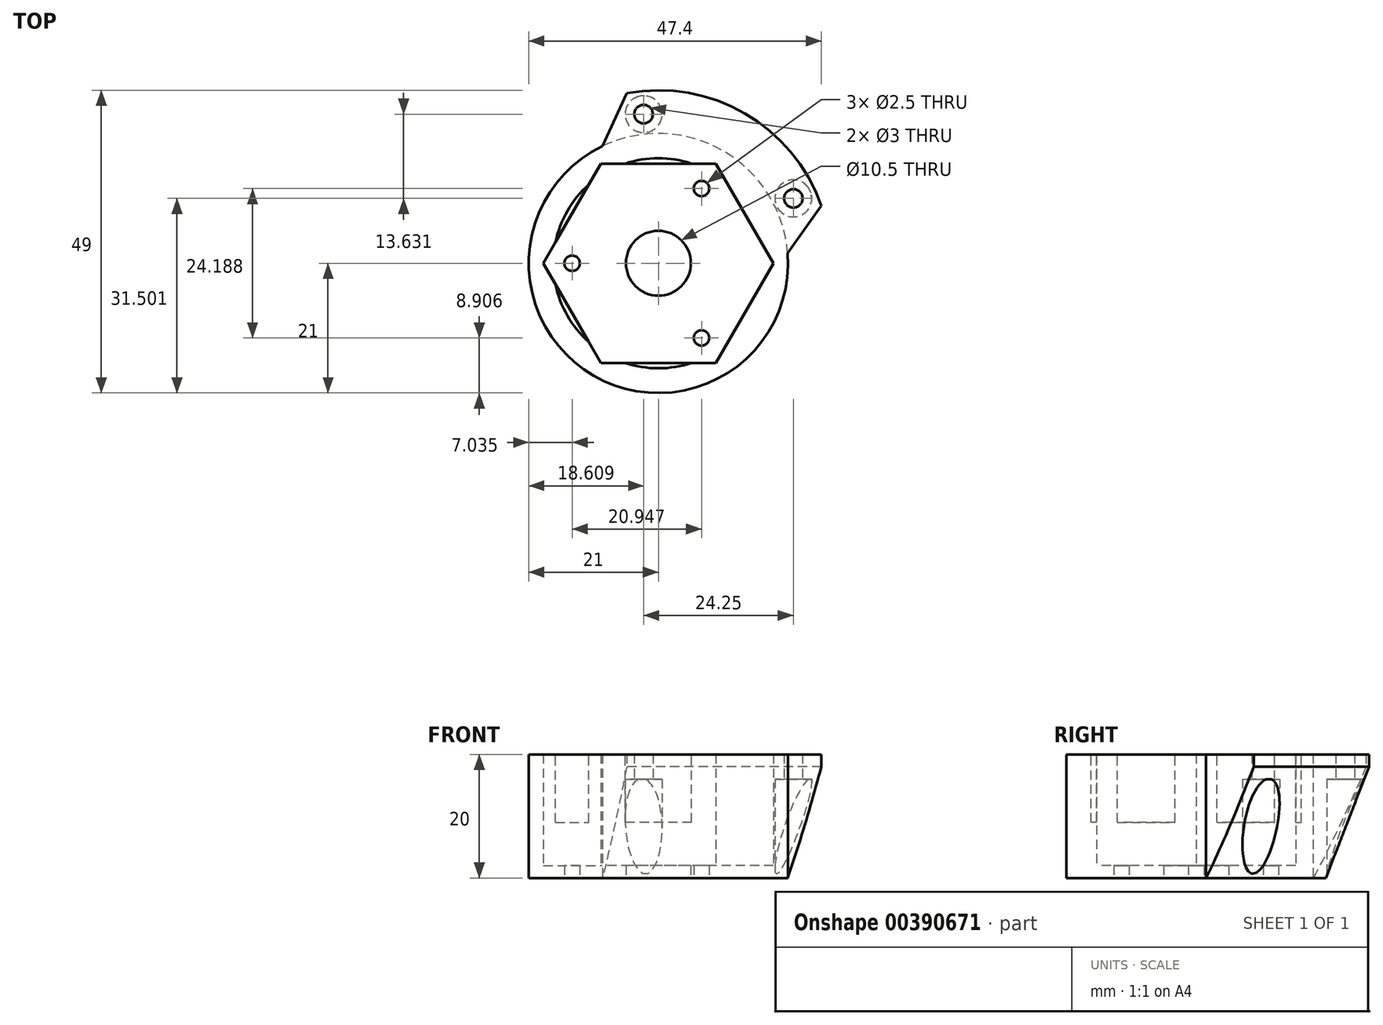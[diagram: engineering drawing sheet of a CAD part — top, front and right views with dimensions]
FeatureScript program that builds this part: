
annotation { "Feature Type Name" : "Feature", "Feature Type Description" : "" }
export const myFeature = defineFeature(function(context is Context, id is Id, definition is map)
    precondition{}
    {
        {
            var Q0;
            Q0=qCreatedBy(makeId("Top.planeOp"),FACE);
            var sketch = newSketch(context, id + "F0", { "sketchPlane" : qUnion([Q0])});
            skCircle(sketch, "E0.cCircle", {"center": v(0, 0) * mm, "radius": 16.12 * mm, "construction": true});
            skLineSegment(sketch, "E0.0", {"start": v(9.3, -16.12) * mm, "end": v(-9.3, -16.13) * mm});
            skLineSegment(sketch, "E0.1", {"start": v(-9.3, -16.12) * mm, "end": v(-18.62, 0) * mm});
            skLineSegment(sketch, "E0.2", {"start": v(-18.62, 0) * mm, "end": v(-9.3, 16.13) * mm});
            skLineSegment(sketch, "E0.3", {"start": v(-9.3, 16.12) * mm, "end": v(9.3, 16.13) * mm});
            skLineSegment(sketch, "E0.4", {"start": v(9.3, 16.12) * mm, "end": v(18.62, 0) * mm});
            skLineSegment(sketch, "E0.5", {"start": v(18.62, 0) * mm, "end": v(9.3, -16.13) * mm});
            skPoint(sketch, "E0.0.midPoint", {"position": v(0, -16.13) * mm});
            skCircle(sketch, "E1", {"center": v(0, 0) * mm, "radius": 5.25 * mm});
            skCircle(sketch, "E2", {"center": v(0, 0) * mm, "radius": 21 * mm});
            skCircle(sketch, "E3", {"center": v(0, 0) * mm, "radius": 28 * mm});
            skCircle(sketch, "E4", {"center": v(-13.96, 0) * mm, "radius": 1.25 * mm});
            skPoint(sketch, "E4.centerSnap0", {"position": v(-13.96, 8.06) * mm});
            skCircle(sketch, "E5.1.0", {"center": v(6.98, -12.1) * mm, "radius": 1.25 * mm});
            skCircle(sketch, "E5.2.0", {"center": v(6.98, 12.1) * mm, "radius": 1.25 * mm});
            skPoint(sketch, "E6.center", {"position": v(-6.44, -15.14) * mm});
            skLineSegment(sketch, "E7", {"start": v(21, 0) * mm, "end": v(28, 0) * mm});
            skLineSegment(sketch, "E8.2.0", {"start": v(-10.5, 18.19) * mm, "end": v(-14, 24.25) * mm});
            skLineSegment(sketch, "E8.anchor1", {"start": v(0, 0) * mm, "end": v(21, 0) * mm, "construction": true});
            skLineSegment(sketch, "E8.anchor2", {"start": v(0, 0) * mm, "end": v(-10.5, 18.19) * mm, "construction": true});
            skSolve(sketch);
        }
        {
            var Q0;
            Q0=makeQuery(id+"F0.imprint","IMPRINT",FACE,{"disambiguationData":[TD([[makeQuery(id+"F0.imprint","IMPRINT",EDGE,{"derivedFrom":sQuery(id+"F0.wireOp",EDGE,"E0.0")}),-1.0]])]});
            extrude(context, id + "F1", {"entities" : qUnion([Q0]), "depth" : 2 * mm});
        }
        {
            var Q0;
            Q0=makeQuery(id+"F0.imprint","IMPRINT",FACE,{"disambiguationData":[TD([[makeQuery(id+"F0.imprint","IMPRINT",EDGE,{"derivedFrom":sQuery(id+"F0.wireOp",EDGE,"E0.0")}),1.0]])]});
            extrude(context, id + "F2", {"entities" : qUnion([Q0]), "operationType" : NewBodyOperationType.ADD, "depth" : 20 * mm});
        }
        {
            var Q0;
            {var subQ0=sQuery(id+"F0.wireOp",EDGE,"E7");Q0=makeQuery(id+"F0.imprint","IMPRINT",FACE,{"disambiguationData":[TD([[makeQuery(id+"F0.imprint","IMPRINT",EDGE,{"derivedFrom":subQ0}),1.0]])]});}
            extrude(context, id + "F3", {"entities" : qUnion([Q0]), "operationType" : NewBodyOperationType.ADD, "depth" : 20 * mm});
        }
        {
            var Q0;
            Q0=makeQuery(id+"F3.opExtrude","SWEPT_EDGE",EDGE,{"disambiguationData":[OSD([sQuery(id+"F0.wireOp",EDGE,"E3"),sQuery(id+"F0.wireOp",EDGE,"E8.2.0")])]});
            var Q1;
            Q1=makeQuery(id+"F3.opExtrude","SWEPT_EDGE",EDGE,{"disambiguationData":[OSD([sQuery(id+"F0.wireOp",EDGE,"E3"),sQuery(id+"F0.wireOp",EDGE,"E7")])]});
            chamfer(context, id + "F4", {"entities" : qUnion([Q0, Q1]), "width" : 7 * mm, "tangentPropagation" : true});
        }
        {
            var Q0;
            Q0=makeQuery(id+"F3.opExtrude","CAP_EDGE",EDGE,{"disambiguationData":[OSD([sQuery(id+"F0.wireOp",EDGE,"E3")])],"isStart":true});
            chamfer(context, id + "F5", {"entities" : qUnion([Q0]), "chamferType" : ChamferType.TWO_OFFSETS, "width1" : 18 * mm, "oppositeDirection" : false, "width2" : 7 * mm, "tangentPropagation" : true});
        }
        {
            var Q0;
            Q0=makeQuery(id+"F0.imprint","IMPRINT",FACE,{"disambiguationData":[TD([[makeQuery(id+"F0.imprint","IMPRINT",EDGE,{"derivedFrom":sQuery(id+"F0.wireOp",EDGE,"E0.0")}),-1.0]])]});
            var sketch = newSketch(context, id + "F6", { "sketchPlane" : qUnion([Q0])});
            skCircle(sketch, "E9", {"center": v(11.88, 21.14) * mm, "radius": 3 * mm});
            skCircle(sketch, "E10", {"center": v(11.88, 21.14) * mm, "radius": 1.5 * mm});
            skCircle(sketch, "E11.1.0", {"center": v(21.86, 10.5) * mm, "radius": 3 * mm});
            skCircle(sketch, "E11.1.1", {"center": v(21.86, 10.5) * mm, "radius": 1.5 * mm});
            skPoint(sketch, "E11.center", {"position": v(0, 0) * mm});
            skLineSegment(sketch, "E11.anchor1", {"start": v(0, 0) * mm, "end": v(11.88, 21.14) * mm, "construction": true});
            skLineSegment(sketch, "E11.anchor2", {"start": v(0, 0) * mm, "end": v(21.86, 10.5) * mm, "construction": true});
            skCircle(sketch, "E12.2.0", {"center": v(-2.4, 24.13) * mm, "radius": 3 * mm});
            skCircle(sketch, "E12.2.1", {"center": v(-2.4, 24.13) * mm, "radius": 1.5 * mm});
            skLineSegment(sketch, "E12.anchor2", {"start": v(0, 0) * mm, "end": v(-2.4, 24.13) * mm, "construction": true});
            skSolve(sketch);
        }
        {
            var Q0;
            Q0=makeQuery(id+"F6.imprint","IMPRINT",FACE,{"disambiguationData":[TD([[makeQuery(id+"F6.imprint","IMPRINT",EDGE,{"derivedFrom":sQuery(id+"F6.wireOp",EDGE,"E11.1.1")}),1.0]])]});
            var Q1;
            Q1=makeQuery(id+"F6.imprint","IMPRINT",FACE,{"disambiguationData":[TD([[makeQuery(id+"F6.imprint","IMPRINT",EDGE,{"derivedFrom":sQuery(id+"F6.wireOp",EDGE,"E12.2.1")}),1.0]])]});
            extrude(context, id + "F7", {"entities" : qUnion([Q0, Q1]), "operationType" : NewBodyOperationType.REMOVE, "depth" : 25 * mm});
        }
        {
            var Q0;
            Q0=makeQuery(id+"F6.imprint","IMPRINT",FACE,{"disambiguationData":[TD([[makeQuery(id+"F6.imprint","IMPRINT",EDGE,{"derivedFrom":sQuery(id+"F6.wireOp",EDGE,"E12.2.0")}),1.0]])]});
            var Q1;
            Q1=makeQuery(id+"F6.imprint","IMPRINT",FACE,{"disambiguationData":[TD([[makeQuery(id+"F6.imprint","IMPRINT",EDGE,{"derivedFrom":sQuery(id+"F6.wireOp",EDGE,"E11.1.0")}),1.0]])]});
            extrude(context, id + "F8", {"entities" : qUnion([Q0, Q1]), "operationType" : NewBodyOperationType.REMOVE, "depth" : 16 * mm});
        }
        {
            var Q0;
            {var subQ0=sQuery(id+"F0.wireOp",EDGE,"E2");Q0=makeQuery(id+"F3.boolean.opBoolean","MERGE",FACE,{"derivedFrom":[makeQuery(id+"F2.opExtrude","CAP_FACE",FACE,{"disambiguationData":[OSD([sQuery(id+"F0.wireOp",EDGE,"E0.0"),sQuery(id+"F0.wireOp",EDGE,"E0.1"),sQuery(id+"F0.wireOp",EDGE,"E0.2"),sQuery(id+"F0.wireOp",EDGE,"E0.3"),sQuery(id+"F0.wireOp",EDGE,"E0.4"),sQuery(id+"F0.wireOp",EDGE,"E0.5"),subQ0])],"isStart":false}),makeQuery(id+"F3.opExtrude","CAP_FACE",FACE,{"disambiguationData":[OSD([subQ0,sQuery(id+"F0.wireOp",EDGE,"E3"),sQuery(id+"F0.wireOp",EDGE,"E7"),sQuery(id+"F0.wireOp",EDGE,"E8.2.0")])],"isStart":false})]});}
            var sketch = newSketch(context, id + "F9", { "sketchPlane" : qUnion([Q0])});
            skCircle(sketch, "E13", {"center": v(0, 0) * mm, "radius": 17 * mm});
            skSolve(sketch);
        }
        {
            var Q0;
            {var subQ0=sQuery(id+"F9.wireOp",EDGE,"E13");var subQ1=makeQuery(id+"F2.opExtrude","CAP_EDGE",EDGE,{"disambiguationData":[OSD([sQuery(id+"F0.wireOp",EDGE,"E0.2")])],"isStart":false});var subQ2=makeQuery(id+"F9.imprint","INTERSECT",VERTEX,{"disambiguationData":[OD(0.0)],"derivedFrom":[subQ1,subQ0]});Q0=makeQuery(id+"F9.imprint","IMPRINT",FACE,{"disambiguationData":[TD([[makeQuery(id+"F9.imprint","IMPRINT",EDGE,{"disambiguationData":[TD([[subQ2,-1.0]])],"derivedFrom":subQ0}),1.0]])]});}
            var Q1;
            {var subQ0=sQuery(id+"F9.wireOp",EDGE,"E13");var subQ1=makeQuery(id+"F2.opExtrude","CAP_EDGE",EDGE,{"disambiguationData":[OSD([sQuery(id+"F0.wireOp",EDGE,"E0.3")])],"isStart":false});var subQ2=makeQuery(id+"F9.imprint","INTERSECT",VERTEX,{"disambiguationData":[OD(0.0)],"derivedFrom":[subQ1,subQ0]});Q1=makeQuery(id+"F9.imprint","IMPRINT",FACE,{"disambiguationData":[TD([[makeQuery(id+"F9.imprint","IMPRINT",EDGE,{"disambiguationData":[TD([[subQ2,-1.0]])],"derivedFrom":subQ0}),1.0]])]});}
            var Q2;
            {var subQ0=sQuery(id+"F9.wireOp",EDGE,"E13");var subQ1=makeQuery(id+"F2.opExtrude","CAP_EDGE",EDGE,{"disambiguationData":[OSD([sQuery(id+"F0.wireOp",EDGE,"E0.4")])],"isStart":false});var subQ2=makeQuery(id+"F9.imprint","INTERSECT",VERTEX,{"disambiguationData":[OD(0.0)],"derivedFrom":[subQ1,subQ0]});Q2=makeQuery(id+"F9.imprint","IMPRINT",FACE,{"disambiguationData":[TD([[makeQuery(id+"F9.imprint","IMPRINT",EDGE,{"disambiguationData":[TD([[subQ2,1.0]])],"derivedFrom":subQ0}),1.0]])]});}
            var Q3;
            {var subQ0=sQuery(id+"F9.wireOp",EDGE,"E13");var subQ1=makeQuery(id+"F2.opExtrude","CAP_EDGE",EDGE,{"disambiguationData":[OSD([sQuery(id+"F0.wireOp",EDGE,"E0.5")])],"isStart":false});var subQ2=makeQuery(id+"F9.imprint","INTERSECT",VERTEX,{"disambiguationData":[OD(0.0)],"derivedFrom":[subQ1,subQ0]});Q3=makeQuery(id+"F9.imprint","IMPRINT",FACE,{"disambiguationData":[TD([[makeQuery(id+"F9.imprint","IMPRINT",EDGE,{"disambiguationData":[TD([[subQ2,-1.0]])],"derivedFrom":subQ0}),1.0]])]});}
            var Q4;
            {var subQ0=sQuery(id+"F9.wireOp",EDGE,"E13");var subQ1=makeQuery(id+"F2.opExtrude","CAP_EDGE",EDGE,{"disambiguationData":[OSD([sQuery(id+"F0.wireOp",EDGE,"E0.0")])],"isStart":false});var subQ2=makeQuery(id+"F9.imprint","INTERSECT",VERTEX,{"disambiguationData":[OD(0.0)],"derivedFrom":[subQ1,subQ0]});Q4=makeQuery(id+"F9.imprint","IMPRINT",FACE,{"disambiguationData":[TD([[makeQuery(id+"F9.imprint","IMPRINT",EDGE,{"disambiguationData":[TD([[subQ2,-1.0]])],"derivedFrom":subQ0}),1.0]])]});}
            var Q5;
            {var subQ0=sQuery(id+"F9.wireOp",EDGE,"E13");var subQ1=makeQuery(id+"F2.opExtrude","CAP_EDGE",EDGE,{"disambiguationData":[OSD([sQuery(id+"F0.wireOp",EDGE,"E0.1")])],"isStart":false});var subQ2=makeQuery(id+"F9.imprint","INTERSECT",VERTEX,{"disambiguationData":[OD(0.0)],"derivedFrom":[subQ1,subQ0]});Q5=makeQuery(id+"F9.imprint","IMPRINT",FACE,{"disambiguationData":[TD([[makeQuery(id+"F9.imprint","IMPRINT",EDGE,{"disambiguationData":[TD([[subQ2,-1.0]])],"derivedFrom":subQ0}),1.0]])]});}
            var Q6;
            Q6=sQuery(id+"F9.wireOp",EDGE,"E13");
            extrude(context, id + "F10", {"entities" : qUnion([Q0, Q1, Q2, Q3, Q4, Q5]), "operationType" : NewBodyOperationType.REMOVE, "surfaceEntities" : qUnion([Q6]), "oppositeDirection" : true, "depth" : 11 * mm});
        }
    });
